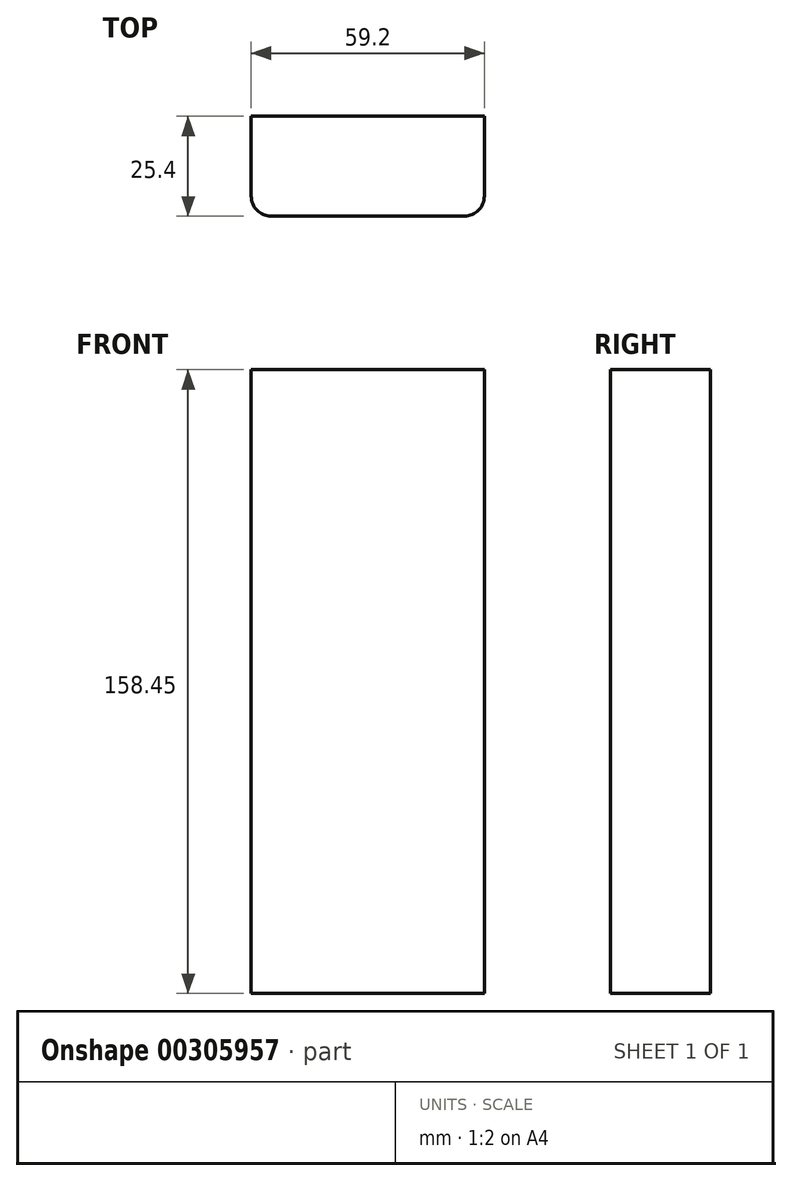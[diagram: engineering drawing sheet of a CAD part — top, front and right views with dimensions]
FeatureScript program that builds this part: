
annotation { "Feature Type Name" : "Feature", "Feature Type Description" : "" }
export const myFeature = defineFeature(function(context is Context, id is Id, definition is map)
    precondition{}
    {
        {
            var Q0;
            Q0=qCreatedBy(makeId("Front.planeOp"),FACE);
            var sketch = newSketch(context, id + "F0", { "sketchPlane" : qUnion([Q0])});
            skLineSegment(sketch, "E0.bottom", {"start": v(-41.44, 55.47) * mm, "end": v(17.76, 55.47) * mm});
            skLineSegment(sketch, "E0.top", {"start": v(-41.44, -102.98) * mm, "end": v(17.76, -102.98) * mm});
            skLineSegment(sketch, "E0.left", {"start": v(-41.44, 55.47) * mm, "end": v(-41.44, -102.98) * mm});
            skLineSegment(sketch, "E0.right", {"start": v(17.76, 55.47) * mm, "end": v(17.76, -102.98) * mm});
            skSolve(sketch);
        }
        {
            var Q0;
            Q0 = qSketchRegion(id + "F0", true);
            extrude(context, id + "F1", {"entities" : qUnion([Q0]), "depth" : 25.4 * mm});
        }
        {
            var Q0;
            Q0=makeQuery(id+"F1.opExtrude","CAP_EDGE",EDGE,{"disambiguationData":[OSD([sQuery(id+"F0.wireOp",EDGE,"E0.left")])],"isStart":false});
            fillet(context, id + "F2", {"entities" : qUnion([Q0]), "radius" : 5.08 * mm, "tangentPropagation" : true, "allowEdgeOverflow" : false});
        }
        {
            var Q0;
            Q0=makeQuery(id+"F1.opExtrude","CAP_EDGE",EDGE,{"disambiguationData":[OSD([sQuery(id+"F0.wireOp",EDGE,"E0.right")])],"isStart":false});
            fillet(context, id + "F3", {"entities" : qUnion([Q0]), "radius" : 5.08 * mm, "tangentPropagation" : true, "allowEdgeOverflow" : false});
        }
    });
